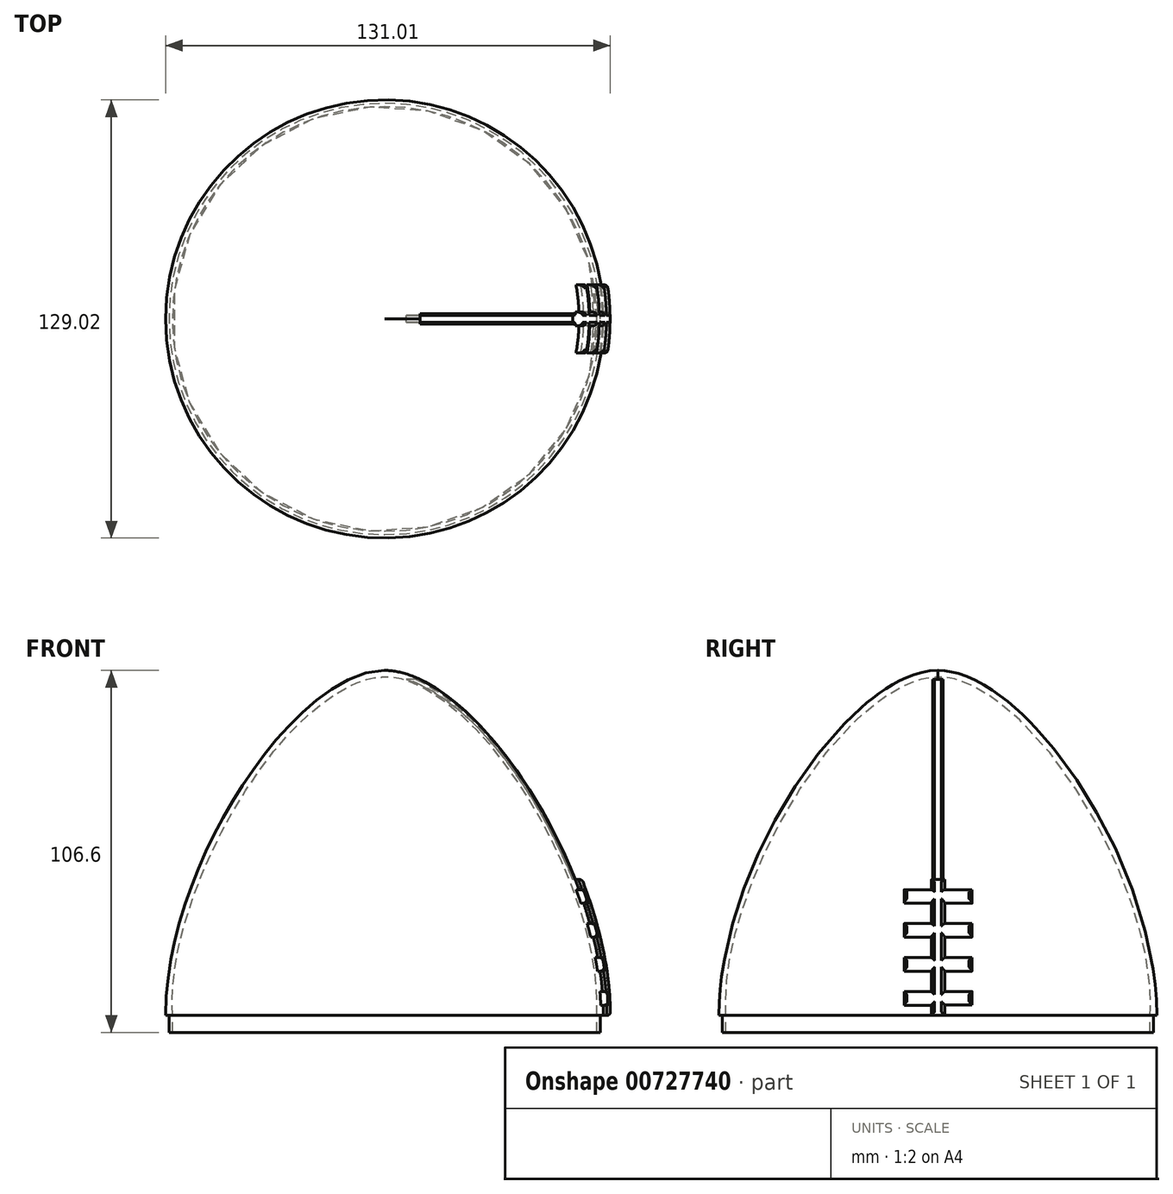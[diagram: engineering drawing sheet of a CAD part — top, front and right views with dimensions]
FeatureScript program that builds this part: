
annotation { "Feature Type Name" : "Feature", "Feature Type Description" : "" }
export const myFeature = defineFeature(function(context is Context, id is Id, definition is map)
    precondition{}
    {
        {
            var Q0;
            Q0=qCreatedBy(makeId("Front.planeOp"),FACE);
            var sketch = newSketch(context, id + "F0", { "sketchPlane" : qUnion([Q0])});
            skPoint(sketch, "E0", {"position": v(64.51, 0) * mm});
            skPoint(sketch, "E1", {"position": v(0, 101.6) * mm});
            skFitSpline(sketch, "E2", {"points": [v(64.51, 0) * mm, v(0, 101.6) * mm], "startDerivative": vector(0, 134.01) * mm, "endDerivative": vector(-78.12, 0) * mm});
            skLineSegment(sketch, "E3", {"start": v(64.51, 0) * mm, "end": v(64.51, 71.79) * mm, "construction": true});
            skLineSegment(sketch, "E4", {"start": v(0, 101.6) * mm, "end": v(55.87, 101.6) * mm, "construction": true});
            skLineSegment(sketch, "E5", {"start": v(0, 108.72) * mm, "end": v(0, 0) * mm});
            skFitSpline(sketch, "E6.0", {"points": [v(62.51, 0) * mm, v(62.51, 5.44) * mm, v(61.34, 16.75) * mm, v(56.6, 34.14) * mm, v(49.47, 51.1) * mm, v(40.54, 66.81) * mm, v(30.43, 80.42) * mm, v(21.54, 89.32) * mm, v(14.5, 94.55) * mm, v(9.37, 97.44) * mm, v(4.47, 99.2) * mm, v(1.45, 99.6) * mm, v(0, 99.6) * mm]});
            skLineSegment(sketch, "E7", {"start": v(0, 101.6) * mm, "end": v(0, 99.6) * mm});
            skLineSegment(sketch, "E8", {"start": v(64.51, 0) * mm, "end": v(62.51, 0) * mm});
            skLineSegment(sketch, "E9", {"start": v(63.51, 0) * mm, "end": v(63.51, -5) * mm});
            skLineSegment(sketch, "E10", {"start": v(62.51, 0) * mm, "end": v(62.51, -5) * mm});
            skLineSegment(sketch, "E11", {"start": v(62.51, -5) * mm, "end": v(63.51, -5) * mm});
            skSolve(sketch);
        }
        {
            var Q0;
            Q0=qCreatedBy(makeId("Right.planeOp"),FACE);
            var sketch = newSketch(context, id + "F1", { "sketchPlane" : qUnion([Q0])});
            skLineSegment(sketch, "E12", {"start": v(2, 0) * mm, "end": v(2, 40) * mm});
            skLineSegment(sketch, "E13", {"start": v(2, 40) * mm, "end": v(0, 40) * mm});
            skLineSegment(sketch, "E14.MirrorCS", {"start": v(-2, 0) * mm, "end": v(-2, 40) * mm});
            skLineSegment(sketch, "E15.MirrorCS", {"start": v(-2, 40) * mm, "end": v(0, 40) * mm});
            skLineSegment(sketch, "E16", {"start": v(2, 3.04) * mm, "end": v(10, 3.04) * mm});
            skLineSegment(sketch, "E17", {"start": v(10, 3.04) * mm, "end": v(10, 7.04) * mm});
            skLineSegment(sketch, "E18", {"start": v(10, 7.04) * mm, "end": v(2, 7.04) * mm});
            skLineSegment(sketch, "E19.MirrorCS", {"start": v(-10, 7.04) * mm, "end": v(-2, 7.04) * mm});
            skLineSegment(sketch, "E20.MirrorCS", {"start": v(-10, 3) * mm, "end": v(-10, 7.04) * mm});
            skLineSegment(sketch, "E21.MirrorCS", {"start": v(-2, 3) * mm, "end": v(-10, 3) * mm});
            skLineSegment(sketch, "E22", {"start": v(2, 13.04) * mm, "end": v(10, 13.04) * mm});
            skLineSegment(sketch, "E23", {"start": v(10, 13.04) * mm, "end": v(10, 17.04) * mm});
            skLineSegment(sketch, "E24", {"start": v(10, 17.04) * mm, "end": v(2, 17.04) * mm});
            skLineSegment(sketch, "E25.MirrorCS", {"start": v(-10, 17.04) * mm, "end": v(-2, 17.04) * mm});
            skLineSegment(sketch, "E26.MirrorCS", {"start": v(-10, 13.04) * mm, "end": v(-10, 17.04) * mm});
            skLineSegment(sketch, "E27.MirrorCS", {"start": v(-2, 13.04) * mm, "end": v(-10, 13.04) * mm});
            skLineSegment(sketch, "E28", {"start": v(2, 23.04) * mm, "end": v(10, 23.04) * mm});
            skLineSegment(sketch, "E29", {"start": v(10, 23.04) * mm, "end": v(10, 27.04) * mm});
            skLineSegment(sketch, "E30", {"start": v(10, 27.04) * mm, "end": v(2, 27.04) * mm});
            skLineSegment(sketch, "E31.MirrorCS", {"start": v(-10, 27.04) * mm, "end": v(-2, 27.04) * mm});
            skLineSegment(sketch, "E32.MirrorCS", {"start": v(-2, 23.04) * mm, "end": v(-10, 23.04) * mm});
            skLineSegment(sketch, "E33.MirrorCS", {"start": v(-10, 23.04) * mm, "end": v(-10, 27.04) * mm});
            skLineSegment(sketch, "E34", {"start": v(-2, 0) * mm, "end": v(2, 0) * mm});
            skLineSegment(sketch, "E35.MirrorCS", {"start": v(-10, 37.04) * mm, "end": v(-2, 37.04) * mm});
            skLineSegment(sketch, "E36.MirrorCS", {"start": v(-2, 33.04) * mm, "end": v(-10, 33.04) * mm});
            skLineSegment(sketch, "E37.MirrorCS", {"start": v(-10, 33.04) * mm, "end": v(-10, 37.04) * mm});
            skLineSegment(sketch, "E38.MirrorCS", {"start": v(2, 33.04) * mm, "end": v(10, 33.04) * mm});
            skLineSegment(sketch, "E39.MirrorCS", {"start": v(10, 37.04) * mm, "end": v(2, 37.04) * mm});
            skLineSegment(sketch, "E40.MirrorCS", {"start": v(10, 33.04) * mm, "end": v(10, 37.04) * mm});
            skSolve(sketch);
        }
        {
            var Q0;
            Q0=qCreatedBy(makeId("Right.planeOp"),FACE);
            cPlane(context, id + "F2", {"entities" : qUnion([Q0]), "cplaneType" : CPlaneType.OFFSET, "offset" : 0 * mm, "width" : 150 * mm, "height" : 150 * mm});
        }
        {
            var Q0;
            Q0=qCreatedBy(id+"F2.planeOp",FACE);
            var sketch = newSketch(context, id + "F3", { "sketchPlane" : qUnion([Q0])});
            skLineSegment(sketch, "E41.0", {"start": v(-2, 40) * mm, "end": v(0, 40) * mm});
            skLineSegment(sketch, "E42.0", {"start": v(2, 40) * mm, "end": v(0, 40) * mm});
            skLineSegment(sketch, "E43", {"start": v(1, 40) * mm, "end": v(1, 98.94) * mm});
            skLineSegment(sketch, "E44", {"start": v(1, 98.94) * mm, "end": v(0, 98.94) * mm});
            skLineSegment(sketch, "E45.MirrorCS", {"start": v(-1, 40) * mm, "end": v(-1, 98.94) * mm});
            skLineSegment(sketch, "E46.MirrorCS", {"start": v(-1, 98.94) * mm, "end": v(0, 98.94) * mm});
            skSolve(sketch);
        }
        {
            var Q0;
            {var subQ1=sQuery(id+"F0.wireOp",EDGE,"E2");Q0=makeQuery(id+"F0.imprint","IMPRINT",FACE,{"disambiguationData":[TD([[makeQuery(id+"F0.imprint","IMPRINT",EDGE,{"derivedFrom":subQ1}),1.0]])]});}
            var Q1;
            {var subQ2=sQuery(id+"F0.wireOp",EDGE,"E9");Q1=makeQuery(id+"F0.imprint","IMPRINT",FACE,{"disambiguationData":[TD([[makeQuery(id+"F0.imprint","IMPRINT",EDGE,{"derivedFrom":subQ2}),-1.0]])]});}
            var Q2;
            Q2=sQuery(id+"F0.wireOp",EDGE,"E5");
            revolve(context, id + "F4", {"surfaceOperationType" : NewSurfaceOperationType.NEW, "entities" : qUnion([Q0, Q1]), "axis" : qUnion([Q2]), "revolveType" : RevolveType.FULL});
        }
        {
            var Q0;
            {var subQ0=sQuery(id+"F1.wireOp",EDGE,"E25.MirrorCS");Q0=makeQuery(id+"F1.imprint","IMPRINT",FACE,{"disambiguationData":[TD([[makeQuery(id+"F1.imprint","IMPRINT",EDGE,{"derivedFrom":subQ0}),-1.0]])]});}
            var Q1;
            {var subQ0=sQuery(id+"F1.wireOp",EDGE,"E19.MirrorCS");Q1=makeQuery(id+"F1.imprint","IMPRINT",FACE,{"disambiguationData":[TD([[makeQuery(id+"F1.imprint","IMPRINT",EDGE,{"derivedFrom":subQ0}),-1.0]])]});}
            var Q2;
            {var subQ0=sQuery(id+"F1.wireOp",EDGE,"E16");Q2=makeQuery(id+"F1.imprint","IMPRINT",FACE,{"disambiguationData":[TD([[makeQuery(id+"F1.imprint","IMPRINT",EDGE,{"derivedFrom":subQ0}),1.0]])]});}
            var Q3;
            {var subQ0=sQuery(id+"F1.wireOp",EDGE,"E22");Q3=makeQuery(id+"F1.imprint","IMPRINT",FACE,{"disambiguationData":[TD([[makeQuery(id+"F1.imprint","IMPRINT",EDGE,{"derivedFrom":subQ0}),1.0]])]});}
            var Q4;
            {var subQ0=sQuery(id+"F1.wireOp",EDGE,"E28");Q4=makeQuery(id+"F1.imprint","IMPRINT",FACE,{"disambiguationData":[TD([[makeQuery(id+"F1.imprint","IMPRINT",EDGE,{"derivedFrom":subQ0}),1.0]])]});}
            var Q5;
            {var subQ0=sQuery(id+"F1.wireOp",EDGE,"E38.MirrorCS");Q5=makeQuery(id+"F1.imprint","IMPRINT",FACE,{"disambiguationData":[TD([[makeQuery(id+"F1.imprint","IMPRINT",EDGE,{"derivedFrom":subQ0}),1.0]])]});}
            var Q6;
            {var subQ0=sQuery(id+"F1.wireOp",EDGE,"E35.MirrorCS");Q6=makeQuery(id+"F1.imprint","IMPRINT",FACE,{"disambiguationData":[TD([[makeQuery(id+"F1.imprint","IMPRINT",EDGE,{"derivedFrom":subQ0}),-1.0]])]});}
            var Q7;
            {var subQ0=sQuery(id+"F1.wireOp",EDGE,"E31.MirrorCS");Q7=makeQuery(id+"F1.imprint","IMPRINT",FACE,{"disambiguationData":[TD([[makeQuery(id+"F1.imprint","IMPRINT",EDGE,{"derivedFrom":subQ0}),-1.0]])]});}
            var Q8;
            {var subQ0=sQuery(id+"F1.wireOp",EDGE,"E13");Q8=makeQuery(id+"F1.imprint","IMPRINT",FACE,{"disambiguationData":[TD([[makeQuery(id+"F1.imprint","IMPRINT",EDGE,{"derivedFrom":subQ0}),1.0]])]});}
            var Q9;
            Q9=makeQuery(id+"F4.opRevolve","SWEPT_FACE",FACE,{"disambiguationData":[OSD([sQuery(id+"F0.wireOp",EDGE,"E2")])]});
            var Q10;
            Q10=makeQuery(id+"F4.opRevolve","SWEPT_BODY",BODY,{"disambiguationData":[OSD([sQuery(id+"F0.wireOp",EDGE,"E2"),sQuery(id+"F0.wireOp",EDGE,"E6.0"),sQuery(id+"F0.wireOp",EDGE,"E7"),sQuery(id+"F0.wireOp",EDGE,"E8"),sQuery(id+"F0.wireOp",EDGE,"E9"),sQuery(id+"F0.wireOp",EDGE,"E10"),sQuery(id+"F0.wireOp",EDGE,"E11")])]});
            extrude(context, id + "F5", {"entities" : qUnion([Q0, Q1, Q2, Q3, Q4, Q5, Q6, Q7, Q8]), "operationType" : NewBodyOperationType.ADD, "endBound" : BoundingType.UP_TO_SURFACE, "depth" : 25 * mm, "endBoundEntityFace" : qUnion([Q9]), "hasOffset" : true, "offsetDistance" : 2 * mm, "offsetOppositeDirection" : true, "hasSecondDirection" : true, "secondDirectionBound" : SecondDirectionBoundingType.UP_TO_BODY, "secondDirectionOppositeDirection" : false, "secondDirectionDepth" : 25 * mm, "secondDirectionBoundEntityBody" : qUnion([Q10])});
        }
        {
            var Q0;
            Q0=makeQuery(id+"F5.opExtrude","CAP_FACE",FACE,{"disambiguationData":[OSD([sQuery(id+"F1.wireOp",EDGE,"E12"),sQuery(id+"F1.wireOp",EDGE,"E13"),sQuery(id+"F1.wireOp",EDGE,"E14.MirrorCS"),sQuery(id+"F1.wireOp",EDGE,"E15.MirrorCS"),sQuery(id+"F1.wireOp",EDGE,"E16"),sQuery(id+"F1.wireOp",EDGE,"E17"),sQuery(id+"F1.wireOp",EDGE,"E18"),sQuery(id+"F1.wireOp",EDGE,"E19.MirrorCS"),sQuery(id+"F1.wireOp",EDGE,"E20.MirrorCS"),sQuery(id+"F1.wireOp",EDGE,"E21.MirrorCS"),sQuery(id+"F1.wireOp",EDGE,"E22"),sQuery(id+"F1.wireOp",EDGE,"E23"),sQuery(id+"F1.wireOp",EDGE,"E24"),sQuery(id+"F1.wireOp",EDGE,"E25.MirrorCS"),sQuery(id+"F1.wireOp",EDGE,"E26.MirrorCS"),sQuery(id+"F1.wireOp",EDGE,"E27.MirrorCS"),sQuery(id+"F1.wireOp",EDGE,"E28"),sQuery(id+"F1.wireOp",EDGE,"E29"),sQuery(id+"F1.wireOp",EDGE,"E30"),sQuery(id+"F1.wireOp",EDGE,"E31.MirrorCS"),sQuery(id+"F1.wireOp",EDGE,"E32.MirrorCS"),sQuery(id+"F1.wireOp",EDGE,"E33.MirrorCS"),sQuery(id+"F1.wireOp",EDGE,"E34"),sQuery(id+"F1.wireOp",EDGE,"E35.MirrorCS"),sQuery(id+"F1.wireOp",EDGE,"E36.MirrorCS"),sQuery(id+"F1.wireOp",EDGE,"E37.MirrorCS"),sQuery(id+"F1.wireOp",EDGE,"E38.MirrorCS"),sQuery(id+"F1.wireOp",EDGE,"E39.MirrorCS"),sQuery(id+"F1.wireOp",EDGE,"E40.MirrorCS")]),topologyDisambiguationEdgeConnected([makeQuery(id+"F4.opRevolve","SWEPT_FACE",FACE,{"disambiguationData":[OSD([sQuery(id+"F0.wireOp",EDGE,"E2")])]})])],"isStart":false});
            var Q1;
            Q1=makeQuery(id+"F5.opExtrude","TWEAK_EDGE",EDGE,{"derivedFrom":[makeQuery(id+"F1.imprint","IMPRINT",EDGE,{"derivedFrom":sQuery(id+"F1.wireOp",EDGE,"E16")}),makeQuery(id+"F1.imprint","IMPRINT",EDGE,{"derivedFrom":sQuery(id+"F1.wireOp",EDGE,"E17")})]});
            var Q2;
            Q2=makeQuery(id+"F5.opExtrude","TWEAK_EDGE",EDGE,{"derivedFrom":[makeQuery(id+"F1.imprint","IMPRINT",EDGE,{"derivedFrom":sQuery(id+"F1.wireOp",EDGE,"E17")}),makeQuery(id+"F1.imprint","IMPRINT",EDGE,{"derivedFrom":sQuery(id+"F1.wireOp",EDGE,"E18")})]});
            var Q3;
            {var subQ0=sQuery(id+"F1.wireOp",EDGE,"E16");var subQ1=sQuery(id+"F1.wireOp",EDGE,"E12");Q3=makeQuery(id+"F5.opExtrude","TWEAK_EDGE",EDGE,{"derivedFrom":[makeQuery(id+"F1.imprint","IMPRINT",EDGE,{"disambiguationData":[TD([[makeQuery(id+"F1.imprint","INTERSECT",VERTEX,{"derivedFrom":[subQ1,sQuery(id+"F1.wireOp",EDGE,"E34")]}),-1.0]])],"derivedFrom":subQ1}),makeQuery(id+"F1.imprint","IMPRINT",EDGE,{"derivedFrom":subQ0})]});}
            var Q4;
            {var subQ0=sQuery(id+"F1.wireOp",EDGE,"E34");var subQ1=sQuery(id+"F1.wireOp",EDGE,"E12");Q4=makeQuery(id+"F5.opExtrude","TWEAK_EDGE",EDGE,{"derivedFrom":[makeQuery(id+"F1.imprint","IMPRINT",EDGE,{"disambiguationData":[TD([[makeQuery(id+"F1.imprint","INTERSECT",VERTEX,{"derivedFrom":[subQ1,subQ0]}),-1.0]])],"derivedFrom":subQ1}),makeQuery(id+"F1.imprint","IMPRINT",EDGE,{"derivedFrom":subQ0})]});}
            var Q5;
            {var subQ0=sQuery(id+"F1.wireOp",EDGE,"E34");var subQ1=sQuery(id+"F1.wireOp",EDGE,"E14.MirrorCS");Q5=makeQuery(id+"F5.opExtrude","TWEAK_EDGE",EDGE,{"derivedFrom":[makeQuery(id+"F1.imprint","IMPRINT",EDGE,{"disambiguationData":[TD([[makeQuery(id+"F1.imprint","INTERSECT",VERTEX,{"derivedFrom":[subQ1,subQ0]}),-1.0]])],"derivedFrom":subQ1}),makeQuery(id+"F1.imprint","IMPRINT",EDGE,{"derivedFrom":subQ0})]});}
            var Q6;
            {var subQ0=sQuery(id+"F1.wireOp",EDGE,"E22");var subQ1=sQuery(id+"F1.wireOp",EDGE,"E12");Q6=makeQuery(id+"F5.opExtrude","TWEAK_EDGE",EDGE,{"derivedFrom":[makeQuery(id+"F1.imprint","IMPRINT",EDGE,{"disambiguationData":[TD([[makeQuery(id+"F1.imprint","INTERSECT",VERTEX,{"derivedFrom":[subQ1,sQuery(id+"F1.wireOp",EDGE,"E18")]}),-1.0]])],"derivedFrom":subQ1}),makeQuery(id+"F1.imprint","IMPRINT",EDGE,{"derivedFrom":subQ0})]});}
            var Q7;
            Q7=makeQuery(id+"F5.opExtrude","TWEAK_EDGE",EDGE,{"derivedFrom":[makeQuery(id+"F1.imprint","IMPRINT",EDGE,{"derivedFrom":sQuery(id+"F1.wireOp",EDGE,"E22")}),makeQuery(id+"F1.imprint","IMPRINT",EDGE,{"derivedFrom":sQuery(id+"F1.wireOp",EDGE,"E23")})]});
            var Q8;
            Q8=makeQuery(id+"F5.opExtrude","TWEAK_EDGE",EDGE,{"derivedFrom":[makeQuery(id+"F1.imprint","IMPRINT",EDGE,{"derivedFrom":sQuery(id+"F1.wireOp",EDGE,"E23")}),makeQuery(id+"F1.imprint","IMPRINT",EDGE,{"derivedFrom":sQuery(id+"F1.wireOp",EDGE,"E24")})]});
            var Q9;
            Q9=makeQuery(id+"F5.opExtrude","TWEAK_EDGE",EDGE,{"derivedFrom":[makeQuery(id+"F1.imprint","IMPRINT",EDGE,{"derivedFrom":sQuery(id+"F1.wireOp",EDGE,"E28")}),makeQuery(id+"F1.imprint","IMPRINT",EDGE,{"derivedFrom":sQuery(id+"F1.wireOp",EDGE,"E29")})]});
            var Q10;
            Q10=makeQuery(id+"F5.opExtrude","TWEAK_EDGE",EDGE,{"derivedFrom":[makeQuery(id+"F1.imprint","IMPRINT",EDGE,{"derivedFrom":sQuery(id+"F1.wireOp",EDGE,"E29")}),makeQuery(id+"F1.imprint","IMPRINT",EDGE,{"derivedFrom":sQuery(id+"F1.wireOp",EDGE,"E30")})]});
            var Q11;
            Q11=makeQuery(id+"F5.opExtrude","TWEAK_EDGE",EDGE,{"derivedFrom":[makeQuery(id+"F1.imprint","IMPRINT",EDGE,{"derivedFrom":sQuery(id+"F1.wireOp",EDGE,"E38.MirrorCS")}),makeQuery(id+"F1.imprint","IMPRINT",EDGE,{"derivedFrom":sQuery(id+"F1.wireOp",EDGE,"E40.MirrorCS")})]});
            var Q12;
            Q12=makeQuery(id+"F5.opExtrude","TWEAK_EDGE",EDGE,{"derivedFrom":[makeQuery(id+"F1.imprint","IMPRINT",EDGE,{"derivedFrom":sQuery(id+"F1.wireOp",EDGE,"E39.MirrorCS")}),makeQuery(id+"F1.imprint","IMPRINT",EDGE,{"derivedFrom":sQuery(id+"F1.wireOp",EDGE,"E40.MirrorCS")})]});
            var Q13;
            {var subQ0=sQuery(id+"F1.wireOp",EDGE,"E38.MirrorCS");var subQ1=sQuery(id+"F1.wireOp",EDGE,"E12");Q13=makeQuery(id+"F5.opExtrude","TWEAK_EDGE",EDGE,{"derivedFrom":[makeQuery(id+"F1.imprint","IMPRINT",EDGE,{"disambiguationData":[TD([[makeQuery(id+"F1.imprint","INTERSECT",VERTEX,{"derivedFrom":[subQ1,sQuery(id+"F1.wireOp",EDGE,"E30")]}),-1.0]])],"derivedFrom":subQ1}),makeQuery(id+"F1.imprint","IMPRINT",EDGE,{"derivedFrom":subQ0})]});}
            var Q14;
            {var subQ0=sQuery(id+"F1.wireOp",EDGE,"E28");var subQ1=sQuery(id+"F1.wireOp",EDGE,"E12");Q14=makeQuery(id+"F5.opExtrude","TWEAK_EDGE",EDGE,{"derivedFrom":[makeQuery(id+"F1.imprint","IMPRINT",EDGE,{"disambiguationData":[TD([[makeQuery(id+"F1.imprint","INTERSECT",VERTEX,{"derivedFrom":[subQ1,sQuery(id+"F1.wireOp",EDGE,"E24")]}),-1.0]])],"derivedFrom":subQ1}),makeQuery(id+"F1.imprint","IMPRINT",EDGE,{"derivedFrom":subQ0})]});}
            var Q15;
            Q15=makeQuery(id+"F5.opExtrude","TWEAK_EDGE",EDGE,{"derivedFrom":[makeQuery(id+"F1.imprint","IMPRINT",EDGE,{"derivedFrom":sQuery(id+"F1.wireOp",EDGE,"E32.MirrorCS")}),makeQuery(id+"F1.imprint","IMPRINT",EDGE,{"derivedFrom":sQuery(id+"F1.wireOp",EDGE,"E33.MirrorCS")})]});
            var Q16;
            Q16=makeQuery(id+"F5.opExtrude","TWEAK_EDGE",EDGE,{"derivedFrom":[makeQuery(id+"F1.imprint","IMPRINT",EDGE,{"derivedFrom":sQuery(id+"F1.wireOp",EDGE,"E36.MirrorCS")}),makeQuery(id+"F1.imprint","IMPRINT",EDGE,{"derivedFrom":sQuery(id+"F1.wireOp",EDGE,"E37.MirrorCS")})]});
            var Q17;
            Q17=makeQuery(id+"F5.opExtrude","TWEAK_EDGE",EDGE,{"derivedFrom":[makeQuery(id+"F1.imprint","IMPRINT",EDGE,{"derivedFrom":sQuery(id+"F1.wireOp",EDGE,"E26.MirrorCS")}),makeQuery(id+"F1.imprint","IMPRINT",EDGE,{"derivedFrom":sQuery(id+"F1.wireOp",EDGE,"E27.MirrorCS")})]});
            var Q18;
            Q18=makeQuery(id+"F5.opExtrude","TWEAK_EDGE",EDGE,{"derivedFrom":[makeQuery(id+"F1.imprint","IMPRINT",EDGE,{"derivedFrom":sQuery(id+"F1.wireOp",EDGE,"E20.MirrorCS")}),makeQuery(id+"F1.imprint","IMPRINT",EDGE,{"derivedFrom":sQuery(id+"F1.wireOp",EDGE,"E21.MirrorCS")})]});
            var Q19;
            {var subQ0=sQuery(id+"F1.wireOp",EDGE,"E18");var subQ1=sQuery(id+"F1.wireOp",EDGE,"E12");Q19=makeQuery(id+"F5.opExtrude","TWEAK_EDGE",EDGE,{"derivedFrom":[makeQuery(id+"F1.imprint","IMPRINT",EDGE,{"disambiguationData":[TD([[makeQuery(id+"F1.imprint","INTERSECT",VERTEX,{"derivedFrom":[subQ1,subQ0]}),-1.0]])],"derivedFrom":subQ1}),makeQuery(id+"F1.imprint","IMPRINT",EDGE,{"derivedFrom":subQ0})]});}
            var Q20;
            {var subQ0=sQuery(id+"F1.wireOp",EDGE,"E24");var subQ1=sQuery(id+"F1.wireOp",EDGE,"E12");Q20=makeQuery(id+"F5.opExtrude","TWEAK_EDGE",EDGE,{"derivedFrom":[makeQuery(id+"F1.imprint","IMPRINT",EDGE,{"disambiguationData":[TD([[makeQuery(id+"F1.imprint","INTERSECT",VERTEX,{"derivedFrom":[subQ1,subQ0]}),-1.0]])],"derivedFrom":subQ1}),makeQuery(id+"F1.imprint","IMPRINT",EDGE,{"derivedFrom":subQ0})]});}
            var Q21;
            {var subQ0=sQuery(id+"F1.wireOp",EDGE,"E30");var subQ1=sQuery(id+"F1.wireOp",EDGE,"E12");Q21=makeQuery(id+"F5.opExtrude","TWEAK_EDGE",EDGE,{"derivedFrom":[makeQuery(id+"F1.imprint","IMPRINT",EDGE,{"disambiguationData":[TD([[makeQuery(id+"F1.imprint","INTERSECT",VERTEX,{"derivedFrom":[subQ1,subQ0]}),-1.0]])],"derivedFrom":subQ1}),makeQuery(id+"F1.imprint","IMPRINT",EDGE,{"derivedFrom":subQ0})]});}
            var Q22;
            {var subQ0=sQuery(id+"F1.wireOp",EDGE,"E39.MirrorCS");var subQ1=sQuery(id+"F1.wireOp",EDGE,"E12");Q22=makeQuery(id+"F5.opExtrude","TWEAK_EDGE",EDGE,{"derivedFrom":[makeQuery(id+"F1.imprint","IMPRINT",EDGE,{"disambiguationData":[TD([[makeQuery(id+"F1.imprint","INTERSECT",VERTEX,{"derivedFrom":[subQ1,sQuery(id+"F1.wireOp",EDGE,"E13")]}),1.0]])],"derivedFrom":subQ1}),makeQuery(id+"F1.imprint","IMPRINT",EDGE,{"derivedFrom":subQ0})]});}
            var Q23;
            {var subQ0=sQuery(id+"F1.wireOp",EDGE,"E13");var subQ1=sQuery(id+"F1.wireOp",EDGE,"E12");Q23=makeQuery(id+"F5.opExtrude","TWEAK_EDGE",EDGE,{"derivedFrom":[makeQuery(id+"F1.imprint","IMPRINT",EDGE,{"disambiguationData":[TD([[makeQuery(id+"F1.imprint","INTERSECT",VERTEX,{"derivedFrom":[subQ1,subQ0]}),1.0]])],"derivedFrom":subQ1}),makeQuery(id+"F1.imprint","IMPRINT",EDGE,{"derivedFrom":subQ0}),makeQuery(id+"F1.imprint","IMPRINT",EDGE,{"derivedFrom":sQuery(id+"F1.wireOp",EDGE,"E15.MirrorCS")})]});}
            var Q24;
            {var subQ0=sQuery(id+"F1.wireOp",EDGE,"E15.MirrorCS");var subQ1=sQuery(id+"F1.wireOp",EDGE,"E14.MirrorCS");Q24=makeQuery(id+"F5.opExtrude","TWEAK_EDGE",EDGE,{"derivedFrom":[makeQuery(id+"F1.imprint","IMPRINT",EDGE,{"derivedFrom":sQuery(id+"F1.wireOp",EDGE,"E13")}),makeQuery(id+"F1.imprint","IMPRINT",EDGE,{"disambiguationData":[TD([[makeQuery(id+"F1.imprint","INTERSECT",VERTEX,{"derivedFrom":[subQ1,subQ0]}),1.0]])],"derivedFrom":subQ1}),makeQuery(id+"F1.imprint","IMPRINT",EDGE,{"derivedFrom":subQ0})]});}
            var Q25;
            Q25=makeQuery(id+"F5.opExtrude","TWEAK_EDGE",EDGE,{"derivedFrom":[makeQuery(id+"F1.imprint","IMPRINT",EDGE,{"derivedFrom":sQuery(id+"F1.wireOp",EDGE,"E35.MirrorCS")}),makeQuery(id+"F1.imprint","IMPRINT",EDGE,{"derivedFrom":sQuery(id+"F1.wireOp",EDGE,"E37.MirrorCS")})]});
            var Q26;
            Q26=makeQuery(id+"F5.opExtrude","TWEAK_EDGE",EDGE,{"derivedFrom":[makeQuery(id+"F1.imprint","IMPRINT",EDGE,{"derivedFrom":sQuery(id+"F1.wireOp",EDGE,"E31.MirrorCS")}),makeQuery(id+"F1.imprint","IMPRINT",EDGE,{"derivedFrom":sQuery(id+"F1.wireOp",EDGE,"E33.MirrorCS")})]});
            var Q27;
            Q27=makeQuery(id+"F5.opExtrude","TWEAK_EDGE",EDGE,{"derivedFrom":[makeQuery(id+"F1.imprint","IMPRINT",EDGE,{"derivedFrom":sQuery(id+"F1.wireOp",EDGE,"E25.MirrorCS")}),makeQuery(id+"F1.imprint","IMPRINT",EDGE,{"derivedFrom":sQuery(id+"F1.wireOp",EDGE,"E26.MirrorCS")})]});
            var Q28;
            Q28=makeQuery(id+"F5.opExtrude","TWEAK_EDGE",EDGE,{"derivedFrom":[makeQuery(id+"F1.imprint","IMPRINT",EDGE,{"derivedFrom":sQuery(id+"F1.wireOp",EDGE,"E19.MirrorCS")}),makeQuery(id+"F1.imprint","IMPRINT",EDGE,{"derivedFrom":sQuery(id+"F1.wireOp",EDGE,"E20.MirrorCS")})]});
            var Q29;
            {var subQ0=sQuery(id+"F1.wireOp",EDGE,"E35.MirrorCS");var subQ1=sQuery(id+"F1.wireOp",EDGE,"E14.MirrorCS");Q29=makeQuery(id+"F5.opExtrude","TWEAK_EDGE",EDGE,{"derivedFrom":[makeQuery(id+"F1.imprint","IMPRINT",EDGE,{"disambiguationData":[TD([[makeQuery(id+"F1.imprint","INTERSECT",VERTEX,{"derivedFrom":[subQ1,sQuery(id+"F1.wireOp",EDGE,"E15.MirrorCS")]}),1.0]])],"derivedFrom":subQ1}),makeQuery(id+"F1.imprint","IMPRINT",EDGE,{"derivedFrom":subQ0})]});}
            var Q30;
            {var subQ0=sQuery(id+"F1.wireOp",EDGE,"E31.MirrorCS");var subQ1=sQuery(id+"F1.wireOp",EDGE,"E14.MirrorCS");Q30=makeQuery(id+"F5.opExtrude","TWEAK_EDGE",EDGE,{"derivedFrom":[makeQuery(id+"F1.imprint","IMPRINT",EDGE,{"disambiguationData":[TD([[makeQuery(id+"F1.imprint","INTERSECT",VERTEX,{"derivedFrom":[subQ1,subQ0]}),-1.0]])],"derivedFrom":subQ1}),makeQuery(id+"F1.imprint","IMPRINT",EDGE,{"derivedFrom":subQ0})]});}
            var Q31;
            {var subQ0=sQuery(id+"F1.wireOp",EDGE,"E25.MirrorCS");var subQ1=sQuery(id+"F1.wireOp",EDGE,"E14.MirrorCS");Q31=makeQuery(id+"F5.opExtrude","TWEAK_EDGE",EDGE,{"derivedFrom":[makeQuery(id+"F1.imprint","IMPRINT",EDGE,{"disambiguationData":[TD([[makeQuery(id+"F1.imprint","INTERSECT",VERTEX,{"derivedFrom":[subQ1,subQ0]}),-1.0]])],"derivedFrom":subQ1}),makeQuery(id+"F1.imprint","IMPRINT",EDGE,{"derivedFrom":subQ0})]});}
            var Q32;
            {var subQ0=sQuery(id+"F1.wireOp",EDGE,"E19.MirrorCS");var subQ1=sQuery(id+"F1.wireOp",EDGE,"E14.MirrorCS");Q32=makeQuery(id+"F5.opExtrude","TWEAK_EDGE",EDGE,{"derivedFrom":[makeQuery(id+"F1.imprint","IMPRINT",EDGE,{"disambiguationData":[TD([[makeQuery(id+"F1.imprint","INTERSECT",VERTEX,{"derivedFrom":[subQ1,subQ0]}),-1.0]])],"derivedFrom":subQ1}),makeQuery(id+"F1.imprint","IMPRINT",EDGE,{"derivedFrom":subQ0})]});}
            var Q33;
            {var subQ0=sQuery(id+"F1.wireOp",EDGE,"E21.MirrorCS");var subQ1=sQuery(id+"F1.wireOp",EDGE,"E14.MirrorCS");Q33=makeQuery(id+"F5.opExtrude","TWEAK_EDGE",EDGE,{"derivedFrom":[makeQuery(id+"F1.imprint","IMPRINT",EDGE,{"disambiguationData":[TD([[makeQuery(id+"F1.imprint","INTERSECT",VERTEX,{"derivedFrom":[subQ1,sQuery(id+"F1.wireOp",EDGE,"E34")]}),-1.0]])],"derivedFrom":subQ1}),makeQuery(id+"F1.imprint","IMPRINT",EDGE,{"derivedFrom":subQ0})]});}
            var Q34;
            {var subQ0=sQuery(id+"F1.wireOp",EDGE,"E27.MirrorCS");var subQ1=sQuery(id+"F1.wireOp",EDGE,"E14.MirrorCS");Q34=makeQuery(id+"F5.opExtrude","TWEAK_EDGE",EDGE,{"derivedFrom":[makeQuery(id+"F1.imprint","IMPRINT",EDGE,{"disambiguationData":[TD([[makeQuery(id+"F1.imprint","INTERSECT",VERTEX,{"derivedFrom":[subQ1,sQuery(id+"F1.wireOp",EDGE,"E19.MirrorCS")]}),-1.0]])],"derivedFrom":subQ1}),makeQuery(id+"F1.imprint","IMPRINT",EDGE,{"derivedFrom":subQ0})]});}
            var Q35;
            {var subQ0=sQuery(id+"F1.wireOp",EDGE,"E32.MirrorCS");var subQ1=sQuery(id+"F1.wireOp",EDGE,"E14.MirrorCS");Q35=makeQuery(id+"F5.opExtrude","TWEAK_EDGE",EDGE,{"derivedFrom":[makeQuery(id+"F1.imprint","IMPRINT",EDGE,{"disambiguationData":[TD([[makeQuery(id+"F1.imprint","INTERSECT",VERTEX,{"derivedFrom":[subQ1,sQuery(id+"F1.wireOp",EDGE,"E25.MirrorCS")]}),-1.0]])],"derivedFrom":subQ1}),makeQuery(id+"F1.imprint","IMPRINT",EDGE,{"derivedFrom":subQ0})]});}
            var Q36;
            {var subQ0=sQuery(id+"F1.wireOp",EDGE,"E36.MirrorCS");var subQ1=sQuery(id+"F1.wireOp",EDGE,"E14.MirrorCS");Q36=makeQuery(id+"F5.opExtrude","TWEAK_EDGE",EDGE,{"derivedFrom":[makeQuery(id+"F1.imprint","IMPRINT",EDGE,{"disambiguationData":[TD([[makeQuery(id+"F1.imprint","INTERSECT",VERTEX,{"derivedFrom":[subQ1,sQuery(id+"F1.wireOp",EDGE,"E31.MirrorCS")]}),-1.0]])],"derivedFrom":subQ1}),makeQuery(id+"F1.imprint","IMPRINT",EDGE,{"derivedFrom":subQ0})]});}
            fillet(context, id + "F6", {"entities" : qUnion([Q0, Q1, Q2, Q3, Q4, Q5, Q6, Q7, Q8, Q9, Q10, Q11, Q12, Q13, Q14, Q15, Q16, Q17, Q18, Q19, Q20, Q21, Q22, Q23, Q24, Q25, Q26, Q27, Q28, Q29, Q30, Q31, Q32, Q33, Q34, Q35, Q36]), "radius" : 1 * mm, "tangentPropagation" : true, "allowEdgeOverflow" : false});
        }
        {
            var Q0;
            {var subQ0=sQuery(id+"F3.wireOp",EDGE,"E43");Q0=makeQuery(id+"F3.imprint","IMPRINT",FACE,{"disambiguationData":[TD([[makeQuery(id+"F3.imprint","IMPRINT",EDGE,{"derivedFrom":subQ0}),1.0]])]});}
            var Q1;
            Q1=makeQuery(id+"F4.opRevolve","SWEPT_FACE",FACE,{"disambiguationData":[OSD([sQuery(id+"F0.wireOp",EDGE,"E2")])]});
            var Q2;
            Q2=makeQuery(id+"F4.opRevolve","SWEPT_BODY",BODY,{"disambiguationData":[OSD([sQuery(id+"F0.wireOp",EDGE,"E2"),sQuery(id+"F0.wireOp",EDGE,"E6.0"),sQuery(id+"F0.wireOp",EDGE,"E7"),sQuery(id+"F0.wireOp",EDGE,"E8"),sQuery(id+"F0.wireOp",EDGE,"E9"),sQuery(id+"F0.wireOp",EDGE,"E10"),sQuery(id+"F0.wireOp",EDGE,"E11")])]});
            extrude(context, id + "F7", {"entities" : qUnion([Q0]), "operationType" : NewBodyOperationType.REMOVE, "endBound" : BoundingType.UP_TO_SURFACE, "depth" : 25 * mm, "endBoundEntityFace" : qUnion([Q1]), "hasOffset" : true, "offsetDistance" : 1 * mm, "offsetOppositeDirection" : true, "hasSecondDirection" : true, "secondDirectionBound" : SecondDirectionBoundingType.UP_TO_BODY, "secondDirectionOppositeDirection" : false, "secondDirectionDepth" : 25 * mm, "secondDirectionBoundEntityBody" : qUnion([Q2]), "hasSecondDirectionOffset" : true, "secondDirectionOffsetDistance" : 1 * mm, "secondDirectionOffsetOppositeDirection" : true});
        }
        {
            var Q0;
            Q0=makeQuery(id+"F7.boolean.opBoolean","INTERSECT",EDGE,{"derivedFrom":[makeQuery(id+"F4.opRevolve","SWEPT_FACE",FACE,{"disambiguationData":[OSD([sQuery(id+"F0.wireOp",EDGE,"E2")])]}),makeQuery(id+"F7.opExtrude","SWEPT_FACE",FACE,{"disambiguationData":[OSD([sQuery(id+"F3.wireOp",EDGE,"E45.MirrorCS")])]})]});
            var Q1;
            Q1=makeQuery(id+"F7.boolean.opBoolean","INTERSECT",EDGE,{"derivedFrom":[makeQuery(id+"F4.opRevolve","SWEPT_FACE",FACE,{"disambiguationData":[OSD([sQuery(id+"F0.wireOp",EDGE,"E2")])]}),makeQuery(id+"F7.opExtrude","SWEPT_FACE",FACE,{"disambiguationData":[OSD([sQuery(id+"F3.wireOp",EDGE,"E43")])]})]});
            var Q2;
            Q2=makeQuery(id+"F7.boolean.opBoolean","COPY",EDGE,{"derivedFrom":makeQuery(id+"F7.opExtrude","CAP_EDGE",EDGE,{"disambiguationData":[OSD([sQuery(id+"F3.wireOp",EDGE,"E43")]),topologyDisambiguationEdgeConnected([makeQuery(id+"F4.opRevolve","SWEPT_FACE",FACE,{"disambiguationData":[OSD([sQuery(id+"F0.wireOp",EDGE,"E6.0")])]})])],"isStart":false})});
            var Q3;
            Q3=makeQuery(id+"F7.boolean.opBoolean","COPY",EDGE,{"derivedFrom":makeQuery(id+"F7.opExtrude","CAP_EDGE",EDGE,{"disambiguationData":[OSD([sQuery(id+"F3.wireOp",EDGE,"E45.MirrorCS")]),topologyDisambiguationEdgeConnected([makeQuery(id+"F4.opRevolve","SWEPT_FACE",FACE,{"disambiguationData":[OSD([sQuery(id+"F0.wireOp",EDGE,"E6.0")])]})])],"isStart":false})});
            fillet(context, id + "F8", {"entities" : qUnion([Q0, Q1, Q2, Q3]), "radius" : .5 * mm, "tangentPropagation" : true, "rho" : 0.5, "crossSection" : FilletCrossSection.CONIC, "allowEdgeOverflow" : false});
        }
    });
